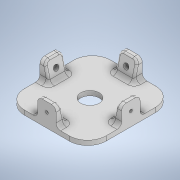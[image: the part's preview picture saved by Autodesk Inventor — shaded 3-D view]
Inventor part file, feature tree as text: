
AUTODESK INVENTOR PART (.ipt)
format: ipt  version: 2021 (Build 250183000, 183)  size: 323,584 bytes
history: native  units: mm
features: sketch x6, extrude x4, fillet x3, plane x2, hole x2, mirror x2, other x1
ambient origin geometry x8: Origin, YZ Plane, XZ Plane, XY Plane, X Axis, Y Axis, Z Axis, Center Point
bodies: Body1 (feature_tree)
feature tree (20):
  other  "實體1"
  extrude  "擠出1"  Depth=89.0mm
  extrude  "擠出2"  Depth=94.0mm
  extrude  "擠出3"  Depth=5.0mm TaperAngle=0.0deg
  plane  "工作平面1"
  hole  "孔1"  [1 undecoded]
  mirror  "鏡射1"
  extrude  "擠出4"  TaperAngle=0.0deg  [1 undecoded]
  plane  "工作平面2"
  hole  "孔2"  [1 undecoded]
  mirror  "鏡射2"
  fillet  "圓角1"  Radius=5.0mm
  fillet  "圓角2"  Radius=10.0mm
  fillet  "圓角3"  Radius=20.0mm
  sketch  "草圖1"
  sketch  "草圖2"
  sketch  "草圖3"
  sketch  "草圖4"
  sketch  "草圖5"
  sketch  "草圖6"
note: 3 required parameter values undecoded (feature->parameter linkage not recoverable at this tier; creation-order binding heuristic only, values carry confidence <= 0.55)
